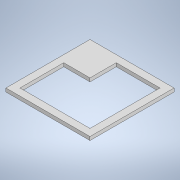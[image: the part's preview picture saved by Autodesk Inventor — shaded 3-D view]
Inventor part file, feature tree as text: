
AUTODESK INVENTOR PART (.ipt)
format: ipt  version: 2020.2 (Build 242310000, 310)  size: 105,472 bytes
history: native  units: mm
features: extrude x1, sketch x1
ambient origin geometry x8: Origin, YZ Plane, XZ Plane, XY Plane, X Axis, Y Axis, Z Axis, Center Point
bodies: Solid1 (feature_tree)
feature tree (2):
  extrude  "Extrusion1"  Depth=2400.0mm
  sketch  "Sketch1"  dims[d0=2400.0mm d1=2400.0mm d2=1250.0mm d3=90.0deg d4=750.0mm d5=750.0mm d6=1250.0mm d7=2000.0mm d8=100.0mm d9=0.0mm]
